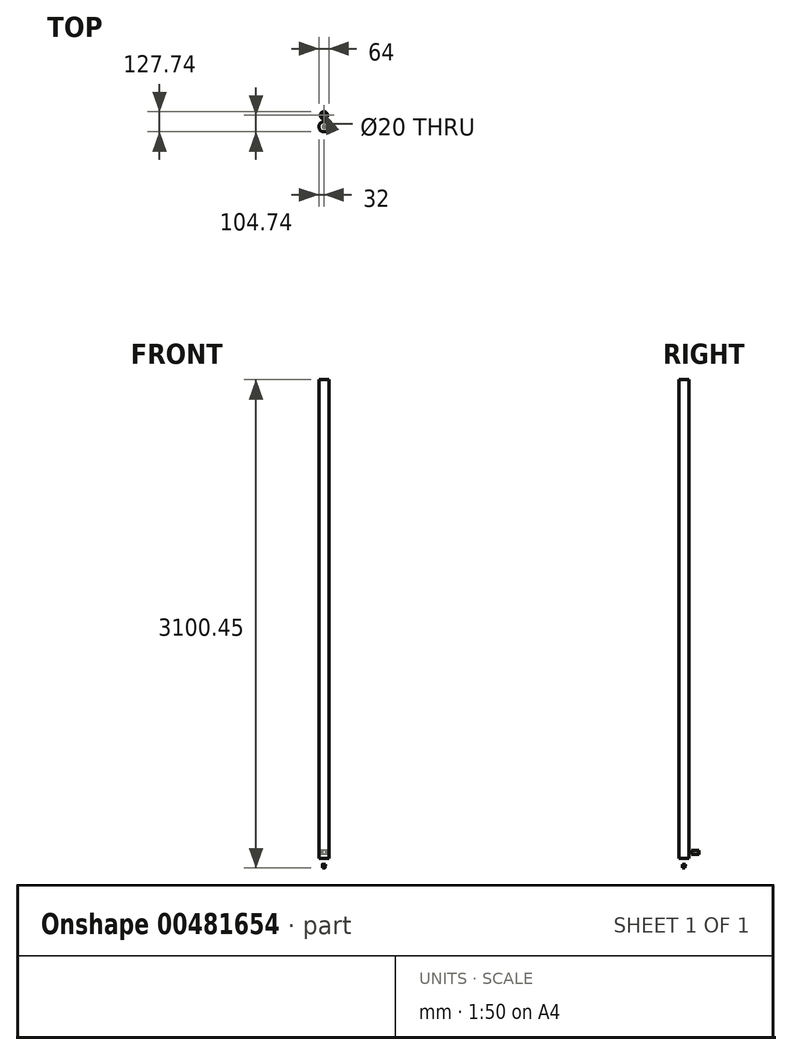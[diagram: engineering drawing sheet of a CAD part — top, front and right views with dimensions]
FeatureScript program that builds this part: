
annotation { "Feature Type Name" : "Feature", "Feature Type Description" : "" }
export const myFeature = defineFeature(function(context is Context, id is Id, definition is map)
    precondition{}
    {
        {
            var Q0;
            Q0=qCreatedBy(makeId("Top.planeOp"),FACE);
            var sketch = newSketch(context, id + "F0", { "sketchPlane" : qUnion([Q0])});
            skCircle(sketch, "E0", {"center": v(0, 0) * mm, "radius": 10 * mm});
            skCircle(sketch, "E1", {"center": v(0, 0) * mm, "radius": 23 * mm});
            skSolve(sketch);
        }
        {
            var Q0;
            Q0=makeQuery(id+"F0.imprint","IMPRINT",FACE,{"disambiguationData":[TD([[makeQuery(id+"F0.imprint","IMPRINT",EDGE,{"derivedFrom":sQuery(id+"F0.wireOp",EDGE,"E0")}),-1.0]])]});
            extrude(context, id + "F1", {"entities" : qUnion([Q0]), "depth" : 25 * mm});
        }
        {
            var Q0;
            Q0=qCreatedBy(makeId("Right.planeOp"),FACE);
            var sketch = newSketch(context, id + "F2", { "sketchPlane" : qUnion([Q0])});
            skLineSegment(sketch, "E2.bottom", {"start": v(-104.74, 3013.73) * mm, "end": v(-72.74, 3013.73) * mm});
            skLineSegment(sketch, "E2.top", {"start": v(-104.74, -26.27) * mm, "end": v(-72.74, -26.27) * mm});
            skLineSegment(sketch, "E2.left", {"start": v(-104.74, 3013.73) * mm, "end": v(-104.74, -26.27) * mm});
            skLineSegment(sketch, "E2.right", {"start": v(-72.74, 3013.73) * mm, "end": v(-72.74, -26.27) * mm});
            skLineSegment(sketch, "E3.bottom", {"start": v(-72.74, -26.27) * mm, "end": v(-82.74, -26.27) * mm});
            skLineSegment(sketch, "E3.top", {"start": v(-72.74, -63.01) * mm, "end": v(-82.74, -63.01) * mm});
            skLineSegment(sketch, "E3.left", {"start": v(-72.74, -26.27) * mm, "end": v(-72.74, -63.01) * mm});
            skLineSegment(sketch, "E3.right", {"start": v(-82.74, -26.27) * mm, "end": v(-82.74, -63.01) * mm});
            skLineSegment(sketch, "E4", {"start": v(-72.74, -63.01) * mm, "end": v(-72.74, -86.72) * mm});
            skLineSegment(sketch, "E5", {"start": v(-72.74, -86.72) * mm, "end": v(-80.24, -86.72) * mm});
            skLineSegment(sketch, "E6", {"start": v(-80.24, -86.72) * mm, "end": v(-82.74, -63.01) * mm});
            skSolve(sketch);
        }
        {
            var Q0;
            Q0=makeQuery(id+"F2.imprint","IMPRINT",FACE,{"disambiguationData":[TD([[makeQuery(id+"F2.imprint","IMPRINT",EDGE,{"derivedFrom":sQuery(id+"F2.wireOp",EDGE,"E3.bottom")}),1.0]])]});
            var Q1;
            Q1=makeQuery(id+"F2.imprint","IMPRINT",FACE,{"disambiguationData":[TD([[makeQuery(id+"F2.imprint","IMPRINT",EDGE,{"derivedFrom":sQuery(id+"F2.wireOp",EDGE,"E3.top")}),1.0]])]});
            var Q2;
            Q2=makeQuery(id+"F2.imprint","IMPRINT",FACE,{"disambiguationData":[TD([[makeQuery(id+"F2.imprint","IMPRINT",EDGE,{"derivedFrom":sQuery(id+"F2.wireOp",EDGE,"E2.bottom")}),-1.0]])]});
            var Q3;
            Q3=sQuery(id+"F2.wireOp",EDGE,"E2.right");
            revolve(context, id + "F3", {"entities" : qUnion([Q0, Q1, Q2]), "axis" : qUnion([Q3]), "revolveType" : RevolveType.FULL});
        }
    });
